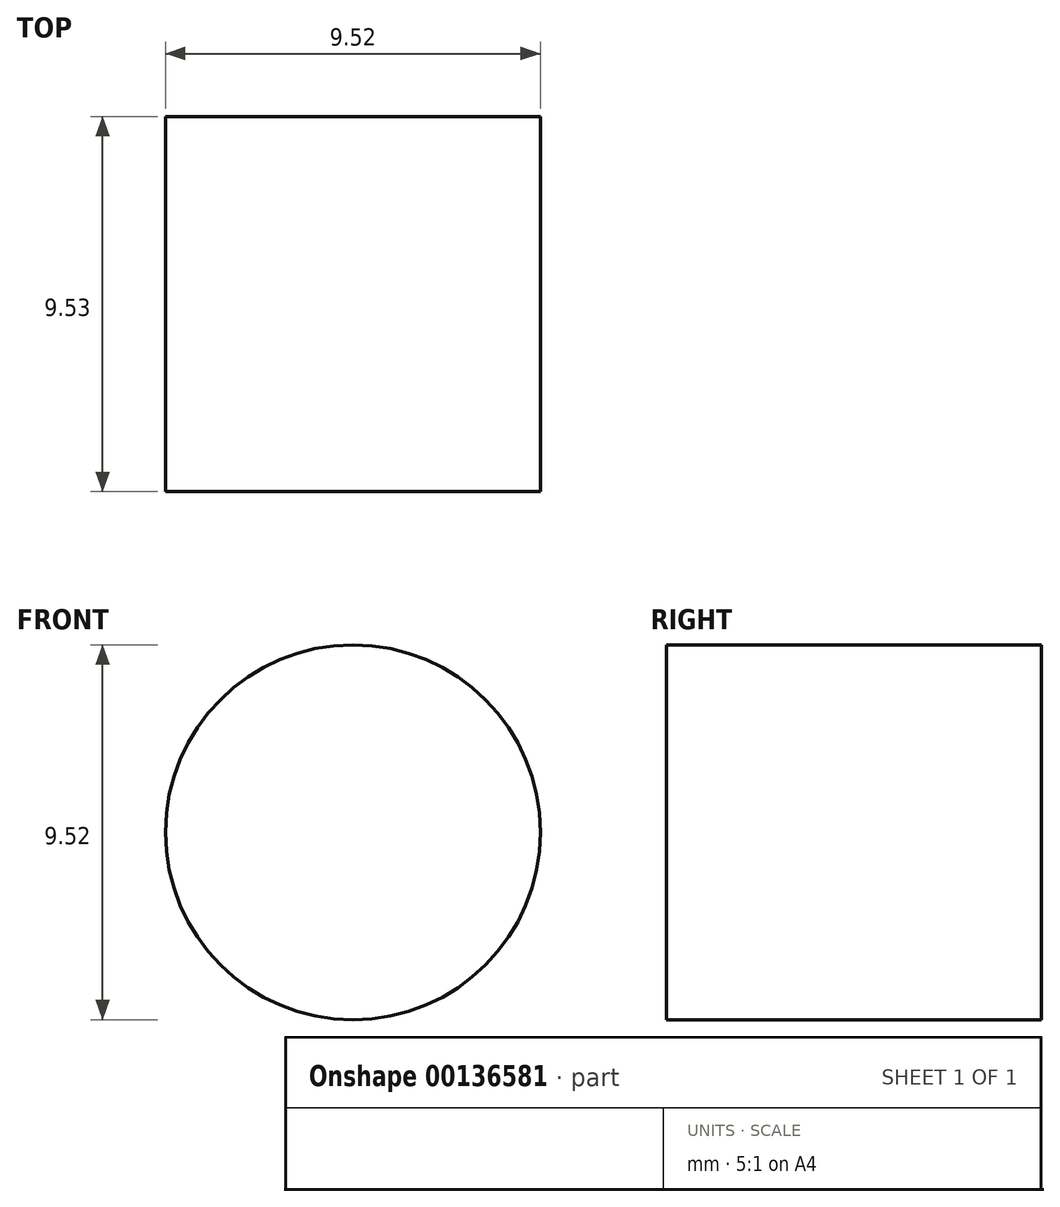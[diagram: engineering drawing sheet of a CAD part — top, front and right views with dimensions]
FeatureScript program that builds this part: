
annotation { "Feature Type Name" : "Feature", "Feature Type Description" : "" }
export const myFeature = defineFeature(function(context is Context, id is Id, definition is map)
    precondition{}
    {
        {
            var Q0;
            Q0=qCreatedBy(makeId("Front.planeOp"),FACE);
            var sketch = newSketch(context, id + "F0", { "sketchPlane" : qUnion([Q0])});
            skCircle(sketch, "E0", {"center": v(0, 0) * mm, "radius": 4.76 * mm});
            skSolve(sketch);
        }
        {
            var Q0;
            Q0=makeQuery(id+"F0.imprint","IMPRINT",FACE,{"disambiguationData":[TD([[makeQuery(id+"F0.imprint","IMPRINT",EDGE,{"derivedFrom":sQuery(id+"F0.wireOp",EDGE,"E0")}),1.0]])]});
            extrude(context, id + "F1", {"entities" : qUnion([Q0]), "depth" : 9.52 * mm});
        }
    });
